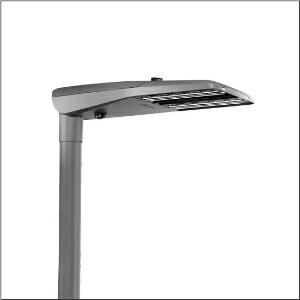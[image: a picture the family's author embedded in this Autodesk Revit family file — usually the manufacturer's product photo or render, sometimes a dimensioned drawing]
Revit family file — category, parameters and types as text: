
# Revit family: streetlight_sl_11_iq_midi___st1_2a_5xc3a51y08me_2b41
name_source: partatom
category: Lighting Fixtures
units: mm (PartAtom-declared; Revit-internal decimal feet)

## family parameters
Cut with Voids When Loaded = No
Host = Face
Light Source = No
Part Type = Normal
Room Calculation Point = No
Round Connector Dimension = Use Diameter
Shared = No

## types (1)
- --- (1 x LED, 18110 lm, 122.7 W, 3000K)
    Apparent Load = 123 VA
    CIE Flux Codes = 32 70 96 100 100
    Color Rendering = 70
    Color Temperature = 3000K
    Default Elevation = 1800 mm
    Description = Streetlight SL 11 iQ midi, mast luminaire, primary light control with 3 zone facetted reflector, of plastic, silver coated, highly specular, primary optical cover: cover, of PMMA, transparent, light distribution: ST1.2a, light emission: direct distribution, primary light characteristic: asymmetric, installation type: post-top, side-entry, LED, High Power LED, rated luminous flux: 18.110lm, luminous efficacy: 148lm/W, light colour: 730, colour temperature: 3000K, control: presetting dimming logarithmic, Street-Remote, Auto-Match, Temp-Guard, Lumen-Switch, Night-Set, Smart-Wire, Light-Fading, Desk-Remote (wireless, voltage-free reading and setting of iQ features in the workshop via application-optimized NFC function/RFID function), optimised constant luminous flux control (CLO 2.0), with cable H07RN-F 5x 1.5mm², mains connection: 230..240V, AC, 50/60Hz, connection cable pre-assembled, cable length: 12,5m, start of lifetime: 123W, end of service life: 130W, reduction: 56W, luminaire housing, of diecast aluminium, powder-coated, Siteco® metallic grey (DB 702S), please order mast flange separately, inclination adjustable without tools: 0°, 5°, 10°, 15° (post-top) | 0°, -5°, -10°, -15° (side-entry), sealing non-destructively replaceable, multi-level sealing system, length: 780mm, width: 376mm, height: 118mm, mast flange for spigot size: 42mm (side-entry): 5XC10008XM4, 60/48mm (side-entry/post-top): 5XC10108XM2, 76/60mm (side-entry/post-top): 5XC10108XM1, equipment: Power, Smart Interface below and above, protection rating (complete): IP66, insulation class (complete): insulation class II (safety insulation), certification: CE, ENEC, VDE, UKCA, impact resistance: IK09, permissible operating ambient temperature for outdoor applications: -25..+50°C, standard-compliant lighting for roads and squares, Environmental Product Declaration (EPD) tested and certified by an independent institute, packaging unit: 1 piece

Light Distribution: ST1.2a
    Height = 118 mm
    Lamp = 1 x LED
    Lamp Light Flux = 18110 lm
    Lamp Power = 122.7 W
    Lamp count = 1
    Length = 780 mm
    Luminous efficacy = 148 lm/W
    Manufacturer = Siteco
    ModVariant = No
    Model = 5XC3A51Y08ME
    Number of Poles = 1
    OnlyDefault = Yes
    Power Factor = 1
    Product Name = Streetlight SL 11 iQ midi | ST1.2a
    Product group = mast luminaire | pylon top
    ProductGroupID = 6100
    Protection Class = Protection class II
    Protection Degree = IP 66
    RLX_Detail_Level = 1
    RLX_Emergency_Light_Flux = 0 lm
    RLX_Emergency_Type = 0
    RLX_Emergency_Type_DB = No
    RlxData = <blob elided: 69853 chars, md5=ad2ccb35>
    Socket = socket
    Standby Power = 0 W
    System Light Flux = 18111 lm
    System Power = 123 W
    Type Comments = factory setting: luminous flux: 100 % | dim-lin: 254 | 553 mA
    Type Image = l_1004429.jpg
    URL = http://relux.com
    VarID = @adj_064599
    Voltage = 0 V
    Weight = 0.00 kg
    Width = 376 mm

## geometry (parser evidence)
native form markers: Blend x4, Sweep x9
no freeform markers — native parametric forms only
